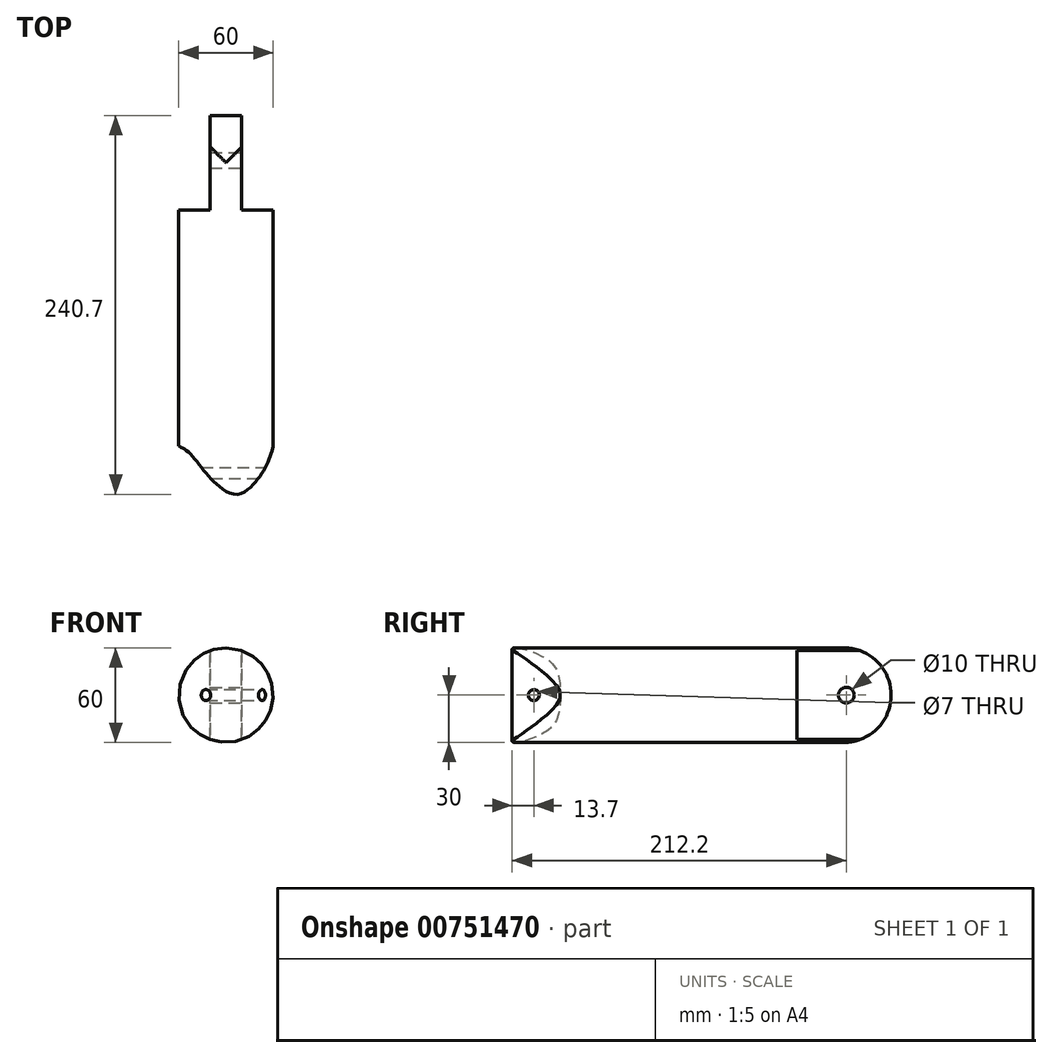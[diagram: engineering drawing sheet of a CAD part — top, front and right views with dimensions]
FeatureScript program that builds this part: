
annotation { "Feature Type Name" : "Feature", "Feature Type Description" : "" }
export const myFeature = defineFeature(function(context is Context, id is Id, definition is map)
    precondition{}
    {
        {
            var Q0;
            Q0=qCreatedBy(makeId("Top.planeOp"),FACE);
            var sketch = newSketch(context, id + "F0", { "sketchPlane" : qUnion([Q0])});
            skLineSegment(sketch, "E0.bottom", {"start": v(0, 75) * mm, "end": v(30, 75) * mm});
            skLineSegment(sketch, "E0.top", {"start": v(0, -75) * mm, "end": v(30, -75) * mm});
            skLineSegment(sketch, "E0.left", {"start": v(0, 75) * mm, "end": v(0, -75) * mm});
            skLineSegment(sketch, "E0.right", {"start": v(30, 75) * mm, "end": v(30, -75) * mm});
            skSolve(sketch);
        }
        {
            var Q0;
            Q0=makeQuery(id+"F0.imprint","IMPRINT",FACE,{"disambiguationData":[TD([[makeQuery(id+"F0.imprint","IMPRINT",EDGE,{"derivedFrom":sQuery(id+"F0.wireOp",EDGE,"E0.bottom")}),-1.0]])]});
            var Q1;
            Q1=sQuery(id+"F0.wireOp",EDGE,"E0.left");
            revolve(context, id + "F1", {"surfaceOperationType" : NewSurfaceOperationType.NEW, "entities" : qUnion([Q0]), "axis" : qUnion([Q1]), "revolveType" : RevolveType.FULL});
        }
        {
            var Q0;
            Q0=qCreatedBy(makeId("Top.planeOp"),FACE);
            var sketch = newSketch(context, id + "F2", { "sketchPlane" : qUnion([Q0])});
            skLineSegment(sketch, "E1", {"start": v(-30, -75) * mm, "end": v(30, -75) * mm});
            skFitSpline(sketch, "E2", {"points": [v(-30, -75) * mm, v(-17.02, -86.8) * mm, v(4.39, -105.5) * mm, v(18.62, -98.02) * mm, v(30, -75) * mm], "startDerivative": vector(87.54, -38.88) * mm, "endDerivative": vector(22.56, 101.8) * mm});
            skSolve(sketch);
        }
        {
            var Q0;
            Q0 = qSketchRegion(id + "F2", true);
            extrude(context, id + "F3", {"entities" : qUnion([Q0]), "endBound" : BoundingType.SYMMETRIC, "depth" : 60 * mm, "offsetDistance" : 25 * mm});
        }
        {
            var Q0;
            Q0=makeQuery(id+"F1.opRevolve","SWEPT_FACE",FACE,{"disambiguationData":[OSD([sQuery(id+"F0.wireOp",EDGE,"E0.bottom")])]});
            extrude(context, id + "F4", {"entities" : qUnion([Q0]), "endBound" : BoundingType.THROUGH_ALL, "oppositeDirection" : true, "depth" : 25 * mm, "offsetDistance" : 25 * mm});
        }
        {
            var Q0;
            Q0=makeQuery(id+"F4.opExtrude","SWEPT_BODY",BODY,{"disambiguationData":[OSD([sQuery(id+"F0.wireOp",EDGE,"E0.bottom")])]});
            var Q1;
            Q1=makeQuery(id+"F3.opExtrude","SWEPT_BODY",BODY,{"disambiguationData":[OSD([sQuery(id+"F2.wireOp",EDGE,"E1"),sQuery(id+"F2.wireOp",EDGE,"E2")])]});
            booleanBodies(context, id + "F5", {"operationType" : BooleanOperationType.INTERSECTION, "tools" : qUnion([Q0, Q1])});
        }
        {
            var Q0;
            Q0=qCreatedBy(makeId("Top.planeOp"),FACE);
            var sketch = newSketch(context, id + "F6", { "sketchPlane" : qUnion([Q0])});
            skLineSegment(sketch, "E3.bottom", {"start": v(0, 150) * mm, "end": v(-10, 150) * mm});
            skLineSegment(sketch, "E3.top", {"start": v(0, 75) * mm, "end": v(-10, 75) * mm});
            skLineSegment(sketch, "E3.left", {"start": v(0, 150) * mm, "end": v(0, 75) * mm});
            skLineSegment(sketch, "E3.right", {"start": v(-10, 150) * mm, "end": v(-10, 75) * mm});
            skLineSegment(sketch, "E4.0.0", {"start": v(-30, 75) * mm, "end": v(30, 75) * mm});
            skLineSegment(sketch, "E5.MirrorCS", {"start": v(30, 75) * mm, "end": v(-30, 75) * mm});
            skLineSegment(sketch, "E6.MirrorCS", {"start": v(0, 75) * mm, "end": v(10, 75) * mm});
            skLineSegment(sketch, "E7.MirrorCS", {"start": v(10, 150) * mm, "end": v(10, 75) * mm});
            skLineSegment(sketch, "E8.MirrorCS", {"start": v(0, 150) * mm, "end": v(10, 150) * mm});
            skSolve(sketch);
        }
        {
            var Q0;
            Q0 = qSketchRegion(id + "F6", true);
            extrude(context, id + "F7", {"entities" : qUnion([Q0]), "endBound" : BoundingType.SYMMETRIC, "depth" : 60 * mm, "offsetDistance" : 25 * mm});
        }
        {
            var Q0;
            Q0=qCreatedBy(makeId("Top.planeOp"),FACE);
            var sketch = newSketch(context, id + "F8", { "sketchPlane" : qUnion([Q0])});
            skLineSegment(sketch, "E9.bottom", {"start": v(0, 75) * mm, "end": v(-30, 75) * mm});
            skLineSegment(sketch, "E9.top", {"start": v(0, 150) * mm, "end": v(-30, 150) * mm});
            skLineSegment(sketch, "E9.left", {"start": v(0, 75) * mm, "end": v(0, 150) * mm});
            skLineSegment(sketch, "E9.right", {"start": v(-30, 75) * mm, "end": v(-30, 150) * mm});
            skLineSegment(sketch, "E10", {"start": v(0, 0) * mm, "end": v(0, 75) * mm, "construction": true});
            skSolve(sketch);
        }
        {
            var Q0;
            Q0 = qSketchRegion(id + "F8", true);
            var Q1;
            Q1=sQuery(id+"F8.wireOp",EDGE,"E9.left");
            revolve(context, id + "F9", {"surfaceOperationType" : NewSurfaceOperationType.NEW, "entities" : qUnion([Q0]), "axis" : qUnion([Q1]), "revolveType" : RevolveType.FULL});
        }
        {
            var Q0;
            Q0=qCreatedBy(makeId("Right.planeOp"),FACE);
            var sketch = newSketch(context, id + "F10", { "sketchPlane" : qUnion([Q0])});
            skLineSegment(sketch, "E11", {"start": v(75, 30) * mm, "end": v(75, -30) * mm});
            skLineSegment(sketch, "E12", {"start": v(75, 30) * mm, "end": v(105, 30) * mm});
            skLineSegment(sketch, "E13", {"start": v(75, -30) * mm, "end": v(105, -30) * mm});
            skArc(sketch, "E14", {"start": v(105, -30) * mm, "mid": v(135, 0) * mm, "end": v(105, 30) * mm});
            skSolve(sketch);
        }
        {
            var Q0;
            Q0 = qSketchRegion(id + "F10", true);
            var Q1;
            Q1=makeQuery(id+"F7.opExtrude","CAP_FACE",FACE,{"disambiguationData":[OSD([sQuery(id+"F6.wireOp",EDGE,"E3.bottom"),sQuery(id+"F6.wireOp",EDGE,"E3.right"),sQuery(id+"F6.wireOp",EDGE,"E7.MirrorCS"),sQuery(id+"F6.wireOp",EDGE,"E5.MirrorCS"),sQuery(id+"F6.wireOp",EDGE,"E8.MirrorCS")])],"isStart":true});
            var Q2;
            Q2=makeQuery(id+"F7.opExtrude","CAP_FACE",FACE,{"disambiguationData":[OSD([sQuery(id+"F6.wireOp",EDGE,"E3.bottom"),sQuery(id+"F6.wireOp",EDGE,"E3.right"),sQuery(id+"F6.wireOp",EDGE,"E7.MirrorCS"),sQuery(id+"F6.wireOp",EDGE,"E5.MirrorCS"),sQuery(id+"F6.wireOp",EDGE,"E8.MirrorCS")])],"isStart":false});
            extrude(context, id + "F11", {"entities" : qUnion([Q0]), "endBound" : BoundingType.SYMMETRIC, "depth" : 60 * mm, "endBoundEntityFace" : qUnion([Q1]), "offsetDistance" : 25 * mm, "hasSecondDirection" : true, "secondDirectionBound" : SecondDirectionBoundingType.UP_TO_SURFACE, "secondDirectionOppositeDirection" : true, "secondDirectionDepth" : 25 * mm, "secondDirectionBoundEntityFace" : qUnion([Q2])});
        }
        {
            var Q0;
            Q0=makeQuery(id+"F7.opExtrude","SWEPT_BODY",BODY,{"disambiguationData":[OSD([sQuery(id+"F6.wireOp",EDGE,"E3.bottom"),sQuery(id+"F6.wireOp",EDGE,"E3.right"),sQuery(id+"F6.wireOp",EDGE,"E7.MirrorCS"),sQuery(id+"F6.wireOp",EDGE,"E5.MirrorCS"),sQuery(id+"F6.wireOp",EDGE,"E8.MirrorCS")])]});
            var Q1;
            Q1=makeQuery(id+"F11.opExtrude","SWEPT_BODY",BODY,{"disambiguationData":[OSD([sQuery(id+"F10.wireOp",EDGE,"vm563JEv-NQ20-3g3q-fMaC-OnRvQP1SJSID"),sQuery(id+"F10.wireOp",EDGE,"E11")])]});
            var Q2;
            Q2=makeQuery(id+"F9.opRevolve","SWEPT_BODY",BODY,{"disambiguationData":[OSD([sQuery(id+"F8.wireOp",EDGE,"E9.bottom"),sQuery(id+"F8.wireOp",EDGE,"E9.top"),sQuery(id+"F8.wireOp",EDGE,"E9.left"),sQuery(id+"F8.wireOp",EDGE,"E9.right")])]});
            booleanBodies(context, id + "F12", {"operationType" : BooleanOperationType.INTERSECTION, "tools" : qUnion([Q0, Q1, Q2])});
        }
        {
            var Q0;
            Q0=makeQuery(id+"F12.opBoolean","INTERSECT",BODY,{"derivedFrom":[makeQuery(id+"F7.opExtrude","SWEPT_BODY",BODY,{"disambiguationData":[OSD([sQuery(id+"F6.wireOp",EDGE,"E3.bottom"),sQuery(id+"F6.wireOp",EDGE,"E3.right"),sQuery(id+"F6.wireOp",EDGE,"E7.MirrorCS"),sQuery(id+"F6.wireOp",EDGE,"E5.MirrorCS"),sQuery(id+"F6.wireOp",EDGE,"E8.MirrorCS")])]}),makeQuery(id+"F9.opRevolve","SWEPT_BODY",BODY,{"disambiguationData":[OSD([sQuery(id+"F8.wireOp",EDGE,"E9.bottom"),sQuery(id+"F8.wireOp",EDGE,"E9.top"),sQuery(id+"F8.wireOp",EDGE,"E9.left"),sQuery(id+"F8.wireOp",EDGE,"E9.right")])]}),makeQuery(id+"F11.opExtrude","SWEPT_BODY",BODY,{"disambiguationData":[OSD([sQuery(id+"F10.wireOp",EDGE,"vm563JEv-NQ20-3g3q-fMaC-OnRvQP1SJSID"),sQuery(id+"F10.wireOp",EDGE,"E11")])]})]});
            var Q1;
            Q1=makeQuery(id+"F5.opBoolean","INTERSECT",BODY,{"derivedFrom":[makeQuery(id+"F3.opExtrude","SWEPT_BODY",BODY,{"disambiguationData":[OSD([sQuery(id+"F2.wireOp",EDGE,"E1"),sQuery(id+"F2.wireOp",EDGE,"E2")])]}),makeQuery(id+"F4.opExtrude","SWEPT_BODY",BODY,{"disambiguationData":[OSD([sQuery(id+"F0.wireOp",EDGE,"E0.bottom")])]})]});
            var Q2;
            Q2=makeQuery(id+"F1.opRevolve","SWEPT_BODY",BODY,{"disambiguationData":[OSD([sQuery(id+"F0.wireOp",EDGE,"E0.bottom"),sQuery(id+"F0.wireOp",EDGE,"E0.top"),sQuery(id+"F0.wireOp",EDGE,"E0.left"),sQuery(id+"F0.wireOp",EDGE,"E0.right")])]});
            booleanBodies(context, id + "F13", {"operationType" : BooleanOperationType.UNION, "tools" : qUnion([Q0, Q1, Q2])});
        }
        {
            var Q0;
            Q0=qCreatedBy(makeId("Right.planeOp"),FACE);
            var sketch = newSketch(context, id + "F14", { "sketchPlane" : qUnion([Q0])});
            skCircle(sketch, "E15", {"center": v(106.5, 0) * mm, "radius": 5 * mm});
            skLineSegment(sketch, "E16", {"start": v(106.5, 0) * mm, "end": v(75, 0) * mm, "construction": true});
            skSolve(sketch);
        }
        {
            var Q0;
            Q0 = qSketchRegion(id + "F14", true);
            extrude(context, id + "F15", {"entities" : qUnion([Q0]), "operationType" : NewBodyOperationType.REMOVE, "endBound" : BoundingType.SYMMETRIC, "oppositeDirection" : true, "depth" : 25 * mm, "offsetDistance" : 25 * mm});
        }
        {
            var Q0;
            Q0=qCreatedBy(makeId("Right.planeOp"),FACE);
            var sketch = newSketch(context, id + "F16", { "sketchPlane" : qUnion([Q0])});
            skCircle(sketch, "E17", {"center": v(-92, 0) * mm, "radius": 3.5 * mm});
            skSolve(sketch);
        }
        {
            var Q0;
            Q0 = qSketchRegion(id + "F16", true);
            extrude(context, id + "F17", {"entities" : qUnion([Q0]), "operationType" : NewBodyOperationType.REMOVE, "endBound" : BoundingType.THROUGH_ALL, "oppositeDirection" : true, "depth" : 25 * mm, "offsetDistance" : 25 * mm, "hasSecondDirection" : true, "secondDirectionBound" : SecondDirectionBoundingType.THROUGH_ALL, "secondDirectionOppositeDirection" : false, "secondDirectionDepth" : 25 * mm});
        }
    });
